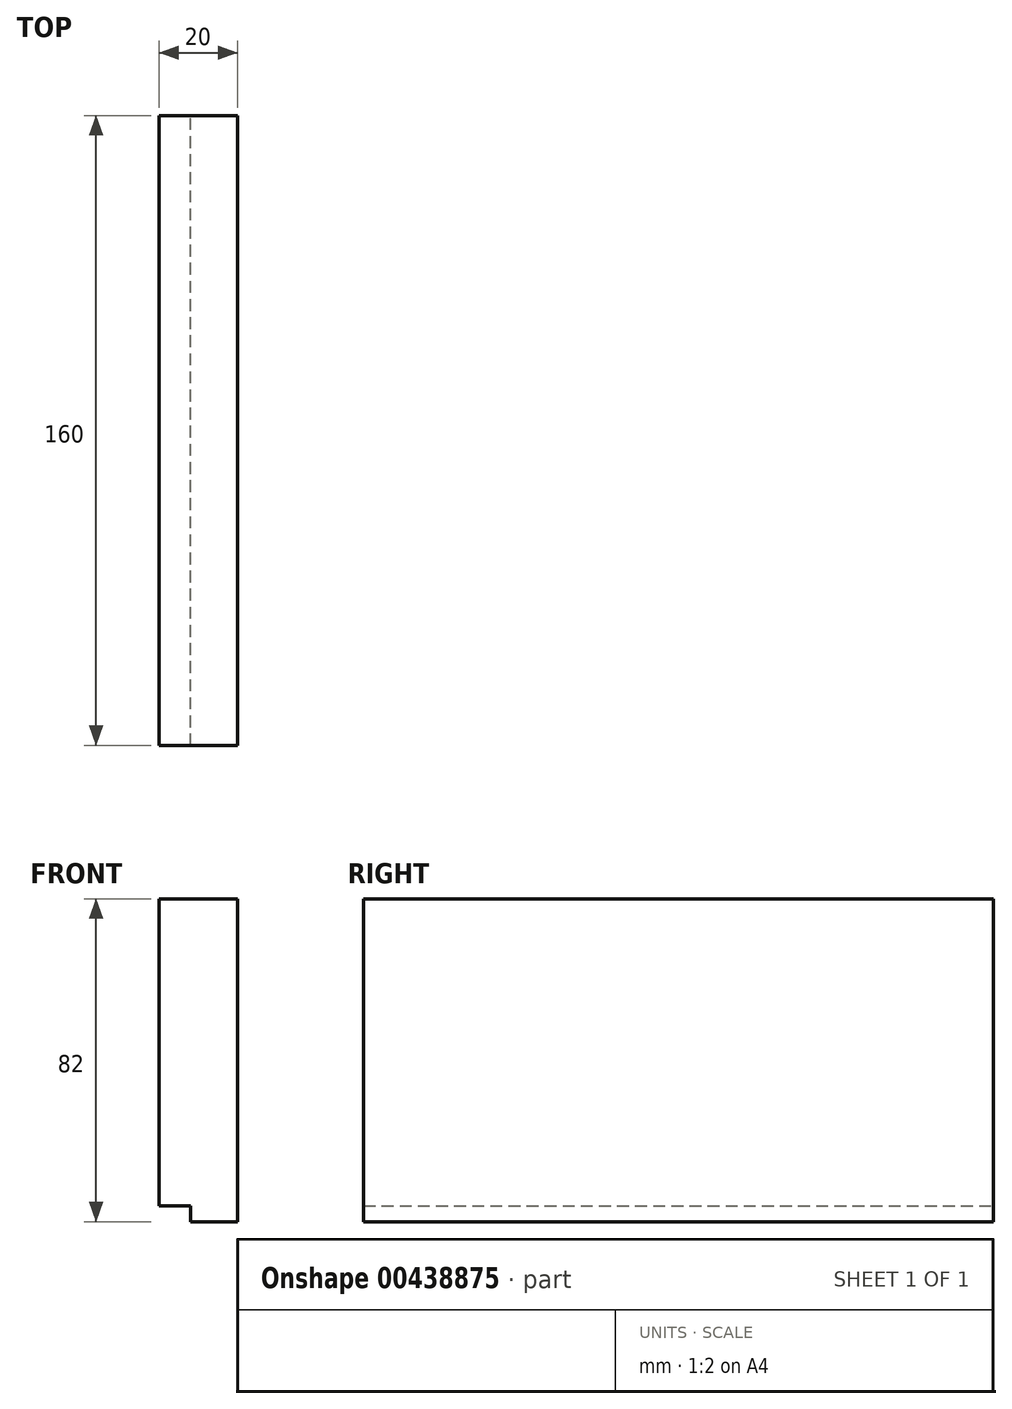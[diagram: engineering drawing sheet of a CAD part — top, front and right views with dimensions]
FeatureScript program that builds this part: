
annotation { "Feature Type Name" : "Feature", "Feature Type Description" : "" }
export const myFeature = defineFeature(function(context is Context, id is Id, definition is map)
    precondition{}
    {
        {
            var Q0;
            Q0=qCreatedBy(makeId("Front.planeOp"),FACE);
            var sketch = newSketch(context, id + "F0", { "sketchPlane" : qUnion([Q0])});
            skLineSegment(sketch, "E0", {"start": v(-76.89, 65.45) * mm, "end": v(-76.89, -12.55) * mm});
            skLineSegment(sketch, "E1", {"start": v(-56.89, -16.55) * mm, "end": v(-68.89, -16.55) * mm});
            skLineSegment(sketch, "E2", {"start": v(-76.89, -12.55) * mm, "end": v(-68.89, -12.55) * mm});
            skLineSegment(sketch, "E3", {"start": v(-68.89, -16.55) * mm, "end": v(-68.89, -12.55) * mm});
            skLineSegment(sketch, "E4", {"start": v(-56.89, -16.55) * mm, "end": v(-56.89, 65.45) * mm});
            skLineSegment(sketch, "E5", {"start": v(-56.89, 65.45) * mm, "end": v(-76.89, 65.45) * mm});
            skSolve(sketch);
        }
        {
            var Q0;
            Q0=makeQuery(id+"F0.imprint","IMPRINT",FACE,{"disambiguationData":[TD([[makeQuery(id+"F0.imprint","IMPRINT",EDGE,{"derivedFrom":sQuery(id+"F0.wireOp",EDGE,"E0")}),1.0]])]});
            extrude(context, id + "F1", {"entities" : qUnion([Q0]), "depth" : 160 * mm});
        }
    });
